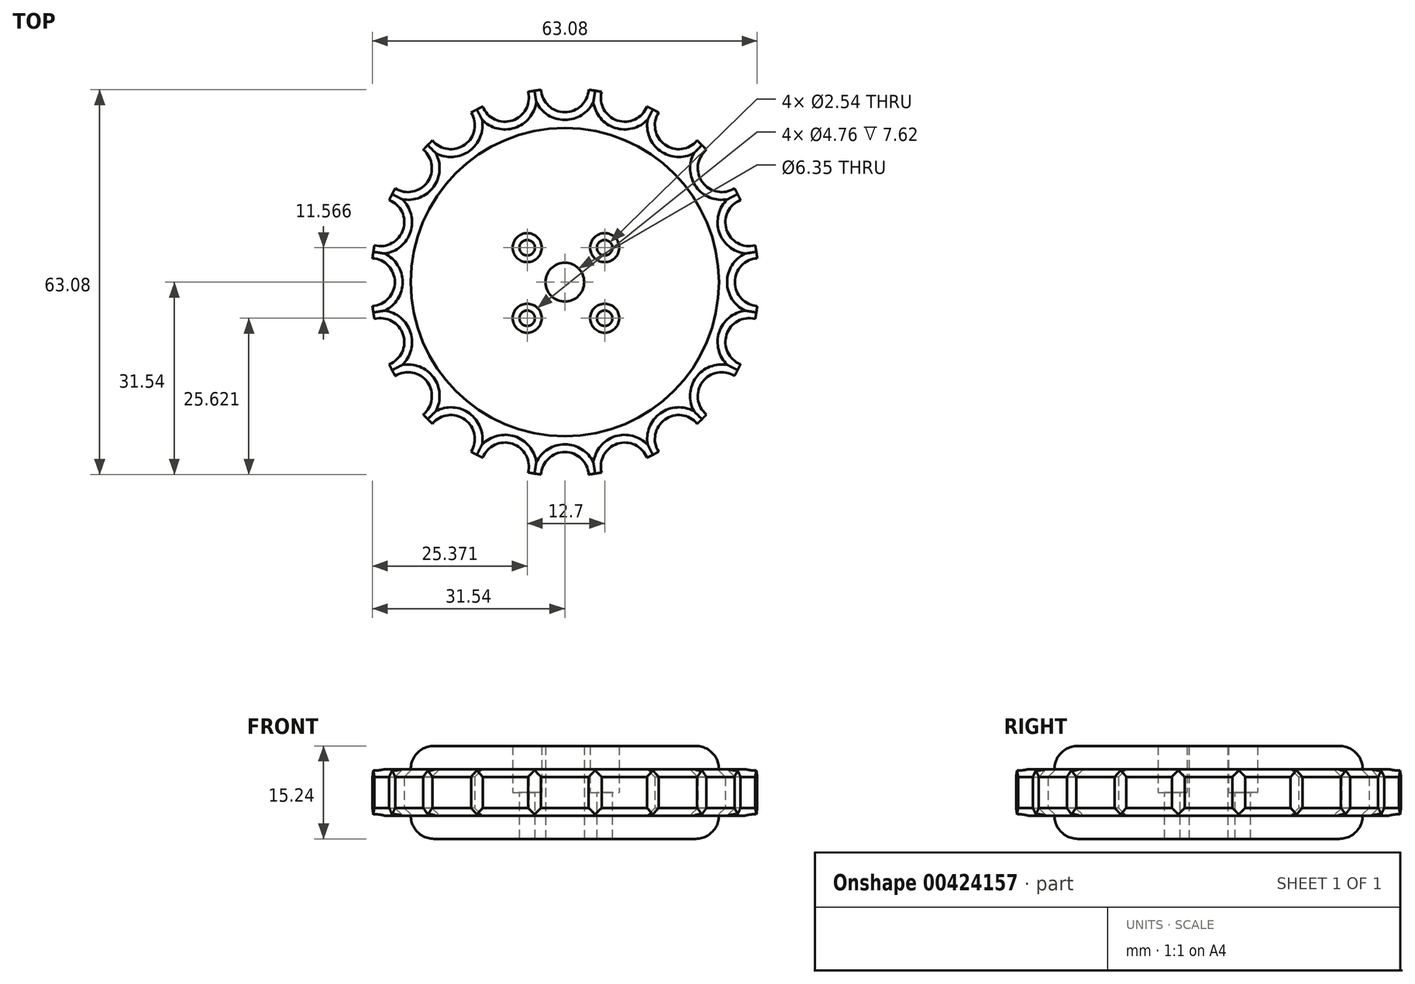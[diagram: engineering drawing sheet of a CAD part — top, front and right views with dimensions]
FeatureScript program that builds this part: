
annotation { "Feature Type Name" : "Feature", "Feature Type Description" : "" }
export const myFeature = defineFeature(function(context is Context, id is Id, definition is map)
    precondition{}
    {
        {
            var Q0;
            Q0=qCreatedBy(makeId("Top.planeOp"),FACE);
            var sketch = newSketch(context, id + "F0", { "sketchPlane" : qUnion([Q0])});
            skCircle(sketch, "E0", {"center": v(0, 0) * mm, "radius": 25.26 * mm});
            skLineSegment(sketch, "E1", {"start": v(0, 0) * mm, "end": v(90.08, 0) * mm, "construction": true});
            skCircle(sketch, "E2", {"center": v(0, 0) * mm, "radius": 31.78 * mm});
            skArc(sketch, "E3", {"start": v(-3.9, 31.54) * mm, "mid": v(0, 27.87) * mm, "end": v(3.9, 31.54) * mm});
            skArc(sketch, "E4.1.0", {"start": v(-13.46, 28.79) * mm, "mid": v(-8.61, 26.5) * mm, "end": v(-6.03, 31.2) * mm});
            skArc(sketch, "E4.2.0", {"start": v(-21.7, 23.22) * mm, "mid": v(-16.38, 22.54) * mm, "end": v(-15.38, 27.81) * mm});
            skArc(sketch, "E4.3.0", {"start": v(-27.81, 15.38) * mm, "mid": v(-22.54, 16.38) * mm, "end": v(-23.22, 21.7) * mm});
            skArc(sketch, "E4.4.0", {"start": v(-31.2, 6.03) * mm, "mid": v(-26.5, 8.61) * mm, "end": v(-28.79, 13.46) * mm});
            skArc(sketch, "E4.5.0", {"start": v(-31.54, -3.9) * mm, "mid": v(-27.87, 0) * mm, "end": v(-31.54, 3.9) * mm});
            skArc(sketch, "E4.6.0", {"start": v(-28.79, -13.46) * mm, "mid": v(-26.5, -8.61) * mm, "end": v(-31.2, -6.03) * mm});
            skArc(sketch, "E4.7.0", {"start": v(-23.22, -21.7) * mm, "mid": v(-22.54, -16.38) * mm, "end": v(-27.81, -15.38) * mm});
            skArc(sketch, "E4.8.0", {"start": v(-15.38, -27.81) * mm, "mid": v(-16.38, -22.54) * mm, "end": v(-21.7, -23.22) * mm});
            skArc(sketch, "E4.9.0", {"start": v(-6.03, -31.2) * mm, "mid": v(-8.61, -26.5) * mm, "end": v(-13.46, -28.79) * mm});
            skArc(sketch, "E4.10.0", {"start": v(3.9, -31.54) * mm, "mid": v(0, -27.87) * mm, "end": v(-3.9, -31.54) * mm});
            skArc(sketch, "E4.11.0", {"start": v(13.46, -28.79) * mm, "mid": v(8.61, -26.5) * mm, "end": v(6.03, -31.2) * mm});
            skArc(sketch, "E4.12.0", {"start": v(21.7, -23.22) * mm, "mid": v(16.38, -22.54) * mm, "end": v(15.38, -27.81) * mm});
            skArc(sketch, "E4.13.0", {"start": v(27.81, -15.38) * mm, "mid": v(22.54, -16.38) * mm, "end": v(23.22, -21.7) * mm});
            skArc(sketch, "E4.14.0", {"start": v(31.2, -6.03) * mm, "mid": v(26.5, -8.61) * mm, "end": v(28.79, -13.46) * mm});
            skArc(sketch, "E4.15.0", {"start": v(31.54, 3.9) * mm, "mid": v(27.87, 0) * mm, "end": v(31.54, -3.9) * mm});
            skArc(sketch, "E4.16.0", {"start": v(28.79, 13.46) * mm, "mid": v(26.5, 8.61) * mm, "end": v(31.2, 6.03) * mm});
            skArc(sketch, "E4.17.0", {"start": v(23.22, 21.7) * mm, "mid": v(22.54, 16.38) * mm, "end": v(27.81, 15.38) * mm});
            skArc(sketch, "E4.18.0", {"start": v(15.38, 27.81) * mm, "mid": v(16.38, 22.54) * mm, "end": v(21.7, 23.22) * mm});
            skArc(sketch, "E4.19.0", {"start": v(6.03, 31.2) * mm, "mid": v(8.61, 26.5) * mm, "end": v(13.46, 28.79) * mm});
            skSolve(sketch);
        }
        {
            var Q0;
            Q0=makeQuery(id+"F0.imprint","IMPRINT",FACE,{"disambiguationData":[TD([[makeQuery(id+"F0.imprint","IMPRINT",EDGE,{"derivedFrom":sQuery(id+"F0.wireOp",EDGE,"E0")}),1.0]])]});
            extrude(context, id + "F1", {"entities" : qUnion([Q0]), "endBound" : BoundingType.SYMMETRIC, "depth" : 15.24 * mm});
        }
        {
            var Q0;
            Q0=sQuery(id+"F0.wireOp",VERTEX,"E1.start");
            var Q1;
            Q1=makeQuery(id+"F1.opExtrude","SWEPT_BODY",BODY,{"disambiguationData":[OSD([sQuery(id+"F0.wireOp",EDGE,"E0")])]});
            hole(context, id + "F2", {"style" : HoleStyle.SIMPLE, "endStyle" : HoleEndStyle.THROUGH, "oppositeDirection" : true, "holeDiameter" : 6.35 * mm, "isTappedThrough" : true, "tappedDepth" : 12.7 * mm, "tapClearance" : 3, "locations" : qUnion([Q0]), "scope" : qUnion([Q1])});
        }
        {
            var Q0;
            Q0=sQuery(id+"F0.wireOp",VERTEX,"E1.start");
            var Q1;
            Q1=makeQuery(id+"F1.opExtrude","SWEPT_BODY",BODY,{"disambiguationData":[OSD([sQuery(id+"F0.wireOp",EDGE,"E0")])]});
            hole(context, id + "F3", {"style" : HoleStyle.SIMPLE, "endStyle" : HoleEndStyle.BLIND, "holeDiameter" : 6.35 * mm, "holeDepth" : 127 * mm, "isTappedThrough" : true, "tappedDepth" : 12.7 * mm, "tapClearance" : 3, "locations" : qUnion([Q0]), "scope" : qUnion([Q1])});
        }
        {
            var Q0;
            Q0=qCreatedBy(makeId("Top.planeOp"),FACE);
            var sketch = newSketch(context, id + "F4", { "sketchPlane" : qUnion([Q0])});
            skLineSegment(sketch, "E5.bottom", {"start": v(-6.17, 5.65) * mm, "end": v(6.53, 5.65) * mm, "construction": true});
            skLineSegment(sketch, "E5.top", {"start": v(-6.17, -5.92) * mm, "end": v(6.53, -5.92) * mm, "construction": true});
            skLineSegment(sketch, "E5.left", {"start": v(-6.17, 5.65) * mm, "end": v(-6.17, -5.92) * mm, "construction": true});
            skLineSegment(sketch, "E5.right", {"start": v(6.53, 5.65) * mm, "end": v(6.53, -5.92) * mm, "construction": true});
            skSolve(sketch);
        }
        {
            var Q0;
            Q0=sQuery(id+"F4.wireOp",VERTEX,"E5.bottom.start");
            var Q1;
            Q1=makeQuery(id+"F1.opExtrude","SWEPT_BODY",BODY,{"disambiguationData":[OSD([sQuery(id+"F0.wireOp",EDGE,"E0")])]});
            hole(context, id + "F5", {"style" : HoleStyle.SIMPLE, "endStyle" : HoleEndStyle.BLIND, "holeDiameter" : 2.54 * mm, "holeDepth" : 127 * mm, "isTappedThrough" : true, "tappedDepth" : 12.7 * mm, "tapClearance" : 3, "locations" : qUnion([Q0]), "scope" : qUnion([Q1])});
        }
        {
            var Q0;
            Q0=sQuery(id+"F4.wireOp",VERTEX,"E5.bottom.start");
            var Q1;
            Q1=makeQuery(id+"F1.opExtrude","SWEPT_BODY",BODY,{"disambiguationData":[OSD([sQuery(id+"F0.wireOp",EDGE,"E0")])]});
            hole(context, id + "F6", {"style" : HoleStyle.SIMPLE, "endStyle" : HoleEndStyle.BLIND, "oppositeDirection" : true, "holeDiameter" : 4.76 * mm, "holeDepth" : 127 * mm, "isTappedThrough" : true, "tappedDepth" : 12.7 * mm, "tapClearance" : 3, "locations" : qUnion([Q0]), "scope" : qUnion([Q1])});
        }
        {
            var Q0;
            Q0=sQuery(id+"F4.wireOp",VERTEX,"E5.left.end");
            var Q1;
            Q1=makeQuery(id+"F1.opExtrude","SWEPT_BODY",BODY,{"disambiguationData":[OSD([sQuery(id+"F0.wireOp",EDGE,"E0")])]});
            hole(context, id + "F7", {"style" : HoleStyle.SIMPLE, "endStyle" : HoleEndStyle.BLIND, "oppositeDirection" : true, "holeDiameter" : 4.76 * mm, "holeDepth" : 127 * mm, "isTappedThrough" : true, "tappedDepth" : 12.7 * mm, "tapClearance" : 3, "locations" : qUnion([Q0]), "scope" : qUnion([Q1])});
        }
        {
            var Q0;
            Q0=sQuery(id+"F4.wireOp",VERTEX,"E5.left.end");
            var Q1;
            Q1=makeQuery(id+"F1.opExtrude","SWEPT_BODY",BODY,{"disambiguationData":[OSD([sQuery(id+"F0.wireOp",EDGE,"E0")])]});
            hole(context, id + "F8", {"style" : HoleStyle.SIMPLE, "endStyle" : HoleEndStyle.BLIND, "holeDiameter" : 2.54 * mm, "holeDepth" : 127 * mm, "isTappedThrough" : true, "tappedDepth" : 12.7 * mm, "tapClearance" : 3, "locations" : qUnion([Q0]), "scope" : qUnion([Q1])});
        }
        {
            var Q0;
            Q0=sQuery(id+"F4.wireOp",VERTEX,"E5.top.end");
            var Q1;
            Q1=makeQuery(id+"F1.opExtrude","SWEPT_BODY",BODY,{"disambiguationData":[OSD([sQuery(id+"F0.wireOp",EDGE,"E0")])]});
            hole(context, id + "F9", {"style" : HoleStyle.SIMPLE, "endStyle" : HoleEndStyle.BLIND, "holeDiameter" : 2.54 * mm, "holeDepth" : 127 * mm, "isTappedThrough" : true, "tappedDepth" : 12.7 * mm, "tapClearance" : 3, "locations" : qUnion([Q0]), "scope" : qUnion([Q1])});
        }
        {
            var Q0;
            Q0=sQuery(id+"F4.wireOp",VERTEX,"E5.top.end");
            var Q1;
            Q1=makeQuery(id+"F1.opExtrude","SWEPT_BODY",BODY,{"disambiguationData":[OSD([sQuery(id+"F0.wireOp",EDGE,"E0")])]});
            hole(context, id + "F10", {"style" : HoleStyle.SIMPLE, "endStyle" : HoleEndStyle.BLIND, "oppositeDirection" : true, "holeDiameter" : 4.76 * mm, "holeDepth" : 127 * mm, "isTappedThrough" : true, "tappedDepth" : 12.7 * mm, "tapClearance" : 3, "locations" : qUnion([Q0]), "scope" : qUnion([Q1])});
        }
        {
            var Q0;
            Q0=sQuery(id+"F4.wireOp",VERTEX,"E5.bottom.end");
            var Q1;
            Q1=makeQuery(id+"F1.opExtrude","SWEPT_BODY",BODY,{"disambiguationData":[OSD([sQuery(id+"F0.wireOp",EDGE,"E0")])]});
            hole(context, id + "F11", {"style" : HoleStyle.SIMPLE, "endStyle" : HoleEndStyle.BLIND, "holeDiameter" : 2.54 * mm, "holeDepth" : 127 * mm, "isTappedThrough" : true, "tappedDepth" : 12.7 * mm, "tapClearance" : 3, "locations" : qUnion([Q0]), "scope" : qUnion([Q1])});
        }
        {
            var Q0;
            Q0=sQuery(id+"F4.wireOp",VERTEX,"E5.bottom.end");
            var Q1;
            Q1=makeQuery(id+"F1.opExtrude","SWEPT_BODY",BODY,{"disambiguationData":[OSD([sQuery(id+"F0.wireOp",EDGE,"E0")])]});
            hole(context, id + "F12", {"style" : HoleStyle.SIMPLE, "endStyle" : HoleEndStyle.BLIND, "oppositeDirection" : true, "holeDiameter" : 4.76 * mm, "holeDepth" : 127 * mm, "isTappedThrough" : true, "tappedDepth" : 12.7 * mm, "tapClearance" : 3, "locations" : qUnion([Q0]), "scope" : qUnion([Q1])});
        }
        {
            var Q0;
            Q0=makeQuery(id+"F1.opExtrude","CAP_EDGE",EDGE,{"disambiguationData":[OSD([sQuery(id+"F0.wireOp",EDGE,"E0")])],"isStart":true});
            fillet(context, id + "F13", {"entities" : qUnion([Q0]), "radius" : 3.8 * mm, "tangentPropagation" : true, "allowEdgeOverflow" : false});
        }
        {
            var Q0;
            Q0=makeQuery(id+"F1.opExtrude","CAP_EDGE",EDGE,{"disambiguationData":[OSD([sQuery(id+"F0.wireOp",EDGE,"E0")])],"isStart":false});
            fillet(context, id + "F14", {"entities" : qUnion([Q0]), "radius" : 3.8 * mm, "tangentPropagation" : true, "allowEdgeOverflow" : false});
        }
        {
            var Q0;
            Q0=makeQuery(id+"F0.imprint","IMPRINT",FACE,{"disambiguationData":[TD([[makeQuery(id+"F0.imprint","IMPRINT",EDGE,{"derivedFrom":sQuery(id+"F0.wireOp",EDGE,"E0")}),-1.0]])]});
            var Q1;
            Q1 = qSketchRegion(id + "FKqvIxa956fVvUm_1", true);
            extrude(context, id + "F15", {"entities" : qUnion([Q0, Q1]), "operationType" : NewBodyOperationType.ADD, "endBound" : BoundingType.SYMMETRIC, "depth" : 7.62 * mm});
        }
        {
            var Q0;
            Q0=makeQuery(id+"F15.opExtrude","CAP_EDGE",EDGE,{"disambiguationData":[OSD([sQuery(id+"F0.wireOp",EDGE,"E4.3.0")])],"isStart":true});
            chamfer(context, id + "F16", {"entities" : qUnion([Q0]), "width" : 1.27 * mm, "tangentPropagation" : true});
        }
        {
            var Q0;
            Q0=makeQuery(id+"F15.opExtrude","CAP_EDGE",EDGE,{"disambiguationData":[OSD([sQuery(id+"F0.wireOp",EDGE,"E4.4.0")])],"isStart":true});
            chamfer(context, id + "F17", {"entities" : qUnion([Q0]), "width" : 1.27 * mm, "tangentPropagation" : true});
        }
        {
            var Q0;
            Q0=makeQuery(id+"F15.opExtrude","CAP_EDGE",EDGE,{"disambiguationData":[OSD([sQuery(id+"F0.wireOp",EDGE,"E4.5.0")])],"isStart":true});
            chamfer(context, id + "F18", {"entities" : qUnion([Q0]), "width" : 1.27 * mm, "tangentPropagation" : true});
        }
        {
            var Q0;
            Q0=makeQuery(id+"F15.opExtrude","CAP_EDGE",EDGE,{"disambiguationData":[OSD([sQuery(id+"F0.wireOp",EDGE,"E4.6.0")])],"isStart":true});
            chamfer(context, id + "F19", {"entities" : qUnion([Q0]), "width" : 1.27 * mm, "tangentPropagation" : true});
        }
        {
            var Q0;
            Q0=makeQuery(id+"F15.opExtrude","CAP_EDGE",EDGE,{"disambiguationData":[OSD([sQuery(id+"F0.wireOp",EDGE,"E4.7.0")])],"isStart":true});
            chamfer(context, id + "F20", {"entities" : qUnion([Q0]), "width" : 1.27 * mm, "tangentPropagation" : true});
        }
        {
            var Q0;
            Q0=makeQuery(id+"F15.opExtrude","CAP_EDGE",EDGE,{"disambiguationData":[OSD([sQuery(id+"F0.wireOp",EDGE,"E4.8.0")])],"isStart":true});
            chamfer(context, id + "F21", {"entities" : qUnion([Q0]), "width" : 1.27 * mm, "tangentPropagation" : true});
        }
        {
            var Q0;
            Q0=makeQuery(id+"F15.opExtrude","CAP_EDGE",EDGE,{"disambiguationData":[OSD([sQuery(id+"F0.wireOp",EDGE,"E4.9.0")])],"isStart":true});
            chamfer(context, id + "F22", {"entities" : qUnion([Q0]), "width" : 1.27 * mm, "tangentPropagation" : true});
        }
        {
            var Q0;
            Q0=makeQuery(id+"F15.opExtrude","CAP_EDGE",EDGE,{"disambiguationData":[OSD([sQuery(id+"F0.wireOp",EDGE,"E4.10.0")])],"isStart":true});
            chamfer(context, id + "F23", {"entities" : qUnion([Q0]), "width" : 1.27 * mm, "tangentPropagation" : true});
        }
        {
            var Q0;
            Q0=makeQuery(id+"F15.opExtrude","CAP_EDGE",EDGE,{"disambiguationData":[OSD([sQuery(id+"F0.wireOp",EDGE,"E4.11.0")])],"isStart":true});
            chamfer(context, id + "F24", {"entities" : qUnion([Q0]), "width" : 1.27 * mm, "tangentPropagation" : true});
        }
        {
            var Q0;
            Q0=makeQuery(id+"F15.opExtrude","CAP_EDGE",EDGE,{"disambiguationData":[OSD([sQuery(id+"F0.wireOp",EDGE,"E4.12.0")])],"isStart":true});
            chamfer(context, id + "F25", {"entities" : qUnion([Q0]), "width" : 1.27 * mm, "tangentPropagation" : true});
        }
        {
            var Q0;
            Q0=makeQuery(id+"F15.opExtrude","CAP_EDGE",EDGE,{"disambiguationData":[OSD([sQuery(id+"F0.wireOp",EDGE,"E4.13.0")])],"isStart":true});
            chamfer(context, id + "F26", {"entities" : qUnion([Q0]), "width" : 1.27 * mm, "tangentPropagation" : true});
        }
        {
            var Q0;
            Q0=makeQuery(id+"F15.opExtrude","CAP_EDGE",EDGE,{"disambiguationData":[OSD([sQuery(id+"F0.wireOp",EDGE,"E4.14.0")])],"isStart":true});
            chamfer(context, id + "F27", {"entities" : qUnion([Q0]), "width" : 1.27 * mm, "tangentPropagation" : true});
        }
        {
            var Q0;
            Q0=makeQuery(id+"F15.opExtrude","CAP_EDGE",EDGE,{"disambiguationData":[OSD([sQuery(id+"F0.wireOp",EDGE,"E4.15.0")])],"isStart":true});
            chamfer(context, id + "F28", {"entities" : qUnion([Q0]), "width" : 1.27 * mm, "tangentPropagation" : true});
        }
        {
            var Q0;
            Q0=makeQuery(id+"F15.opExtrude","CAP_EDGE",EDGE,{"disambiguationData":[OSD([sQuery(id+"F0.wireOp",EDGE,"E4.16.0")])],"isStart":true});
            chamfer(context, id + "F29", {"entities" : qUnion([Q0]), "width" : 1.27 * mm, "tangentPropagation" : true});
        }
        {
            var Q0;
            Q0=makeQuery(id+"F15.opExtrude","CAP_EDGE",EDGE,{"disambiguationData":[OSD([sQuery(id+"F0.wireOp",EDGE,"E4.17.0")])],"isStart":true});
            chamfer(context, id + "F30", {"entities" : qUnion([Q0]), "width" : 1.27 * mm, "tangentPropagation" : true});
        }
        {
            var Q0;
            Q0=makeQuery(id+"F15.opExtrude","CAP_EDGE",EDGE,{"disambiguationData":[OSD([sQuery(id+"F0.wireOp",EDGE,"E4.18.0")])],"isStart":true});
            chamfer(context, id + "F31", {"entities" : qUnion([Q0]), "width" : 1.27 * mm, "tangentPropagation" : true});
        }
        {
            var Q0;
            Q0=makeQuery(id+"F15.opExtrude","CAP_EDGE",EDGE,{"disambiguationData":[OSD([sQuery(id+"F0.wireOp",EDGE,"E4.19.0")])],"isStart":true});
            chamfer(context, id + "F32", {"entities" : qUnion([Q0]), "width" : 1.27 * mm, "tangentPropagation" : true});
        }
        {
            var Q0;
            Q0=makeQuery(id+"F15.opExtrude","CAP_EDGE",EDGE,{"disambiguationData":[OSD([sQuery(id+"F0.wireOp",EDGE,"E3")])],"isStart":true});
            chamfer(context, id + "F33", {"entities" : qUnion([Q0]), "width" : 1.27 * mm, "tangentPropagation" : true});
        }
        {
            var Q0;
            Q0=makeQuery(id+"F15.opExtrude","CAP_EDGE",EDGE,{"disambiguationData":[OSD([sQuery(id+"F0.wireOp",EDGE,"E4.1.0")])],"isStart":true});
            chamfer(context, id + "F34", {"entities" : qUnion([Q0]), "width" : 1.27 * mm, "tangentPropagation" : true});
        }
        {
            var Q0;
            Q0=makeQuery(id+"F15.opExtrude","CAP_EDGE",EDGE,{"disambiguationData":[OSD([sQuery(id+"F0.wireOp",EDGE,"E4.2.0")])],"isStart":true});
            chamfer(context, id + "F35", {"entities" : qUnion([Q0]), "width" : 1.27 * mm, "tangentPropagation" : true});
        }
        {
            var Q0;
            Q0=makeQuery(id+"F15.opExtrude","CAP_EDGE",EDGE,{"disambiguationData":[OSD([sQuery(id+"F0.wireOp",EDGE,"E3")])],"isStart":false});
            var Q1;
            Q1=makeQuery(id+"F15.opExtrude","CAP_EDGE",EDGE,{"disambiguationData":[OSD([sQuery(id+"F0.wireOp",EDGE,"E4.18.0")])],"isStart":false});
            var Q2;
            Q2=makeQuery(id+"F15.opExtrude","CAP_EDGE",EDGE,{"disambiguationData":[OSD([sQuery(id+"F0.wireOp",EDGE,"E4.16.0")])],"isStart":false});
            var Q3;
            Q3=makeQuery(id+"F15.opExtrude","CAP_EDGE",EDGE,{"disambiguationData":[OSD([sQuery(id+"F0.wireOp",EDGE,"E4.14.0")])],"isStart":false});
            var Q4;
            Q4=makeQuery(id+"F15.opExtrude","CAP_EDGE",EDGE,{"disambiguationData":[OSD([sQuery(id+"F0.wireOp",EDGE,"E4.12.0")])],"isStart":false});
            var Q5;
            Q5=makeQuery(id+"F15.opExtrude","CAP_EDGE",EDGE,{"disambiguationData":[OSD([sQuery(id+"F0.wireOp",EDGE,"E4.10.0")])],"isStart":false});
            var Q6;
            Q6=makeQuery(id+"F15.opExtrude","CAP_EDGE",EDGE,{"disambiguationData":[OSD([sQuery(id+"F0.wireOp",EDGE,"E4.8.0")])],"isStart":false});
            var Q7;
            Q7=makeQuery(id+"F15.opExtrude","CAP_EDGE",EDGE,{"disambiguationData":[OSD([sQuery(id+"F0.wireOp",EDGE,"E4.6.0")])],"isStart":false});
            var Q8;
            Q8=makeQuery(id+"F15.opExtrude","CAP_EDGE",EDGE,{"disambiguationData":[OSD([sQuery(id+"F0.wireOp",EDGE,"E4.4.0")])],"isStart":false});
            var Q9;
            Q9=makeQuery(id+"F15.opExtrude","CAP_EDGE",EDGE,{"disambiguationData":[OSD([sQuery(id+"F0.wireOp",EDGE,"E4.2.0")])],"isStart":false});
            chamfer(context, id + "F36", {"entities" : qUnion([Q0, Q1, Q2, Q3, Q4, Q5, Q6, Q7, Q8, Q9]), "width" : 1.27 * mm, "tangentPropagation" : true});
        }
        {
            var Q0;
            Q0=makeQuery(id+"F15.opExtrude","CAP_EDGE",EDGE,{"disambiguationData":[OSD([sQuery(id+"F0.wireOp",EDGE,"E4.1.0")])],"isStart":false});
            var Q1;
            Q1=makeQuery(id+"F15.opExtrude","CAP_EDGE",EDGE,{"disambiguationData":[OSD([sQuery(id+"F0.wireOp",EDGE,"E4.19.0")])],"isStart":false});
            var Q2;
            Q2=makeQuery(id+"F15.opExtrude","CAP_EDGE",EDGE,{"disambiguationData":[OSD([sQuery(id+"F0.wireOp",EDGE,"E4.17.0")])],"isStart":false});
            var Q3;
            Q3=makeQuery(id+"F15.opExtrude","CAP_EDGE",EDGE,{"disambiguationData":[OSD([sQuery(id+"F0.wireOp",EDGE,"E4.15.0")])],"isStart":false});
            var Q4;
            Q4=makeQuery(id+"F15.opExtrude","CAP_EDGE",EDGE,{"disambiguationData":[OSD([sQuery(id+"F0.wireOp",EDGE,"E4.13.0")])],"isStart":false});
            var Q5;
            Q5=makeQuery(id+"F15.opExtrude","CAP_EDGE",EDGE,{"disambiguationData":[OSD([sQuery(id+"F0.wireOp",EDGE,"E4.11.0")])],"isStart":false});
            var Q6;
            Q6=makeQuery(id+"F15.opExtrude","CAP_EDGE",EDGE,{"disambiguationData":[OSD([sQuery(id+"F0.wireOp",EDGE,"E4.9.0")])],"isStart":false});
            var Q7;
            Q7=makeQuery(id+"F15.opExtrude","CAP_EDGE",EDGE,{"disambiguationData":[OSD([sQuery(id+"F0.wireOp",EDGE,"E4.7.0")])],"isStart":false});
            var Q8;
            Q8=makeQuery(id+"F15.opExtrude","CAP_EDGE",EDGE,{"disambiguationData":[OSD([sQuery(id+"F0.wireOp",EDGE,"E4.5.0")])],"isStart":false});
            chamfer(context, id + "F37", {"entities" : qUnion([Q0, Q1, Q2, Q3, Q4, Q5, Q6, Q7, Q8]), "width" : 1.27 * mm, "tangentPropagation" : true});
        }
        {
            var Q0;
            Q0=makeQuery(id+"F15.opExtrude","CAP_EDGE",EDGE,{"disambiguationData":[OSD([sQuery(id+"F0.wireOp",EDGE,"E4.3.0")])],"isStart":false});
            chamfer(context, id + "F38", {"entities" : qUnion([Q0]), "width" : 1.27 * mm, "tangentPropagation" : true});
        }
    });
